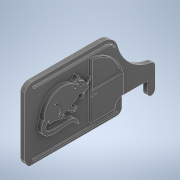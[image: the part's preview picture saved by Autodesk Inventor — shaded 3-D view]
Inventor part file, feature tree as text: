
AUTODESK INVENTOR PART (.ipt)
format: ipt  version: 2022 (Build 260153000, 153)  size: 345,600 bytes
history: native  units: in
note: dims shown in document units (in); Inventor stores cm internally (conversion verified against a paired STEP export)
features: other x5, extrude x3, sketch x1
ambient origin geometry x8: Origin, YZ Plane, XZ Plane, XY Plane, X Axis, Y Axis, Z Axis, Center Point
bodies: Solid1 (feature_tree)
feature tree (9):
  other  "outline"
  extrude  "main right panel"  Depth=0.25in
  other  "rat icon raw"
  extrude  "car details extrusion"  Depth=0.25in
  extrude  "rat extrusion"  Depth=0.25in
  sketch  "Sketch2"  dims[d0=7.0in d1=5.0in d2=1.5in d3=1.75in d4=0.25in d5=0.25in d6=0.25in d7=0.25in d8=0.1875in d9=0.972in d10=5.878in d11=0.25in d12=0.0in d46=0.1in d47=0.0in d48=0.25in d49=0.0in d44=0.5in d45=0.0344in d50=0.5in d51=0.0344in]
  other  "detail lines"
  other  "Image1"
  other  "rat sketch"
